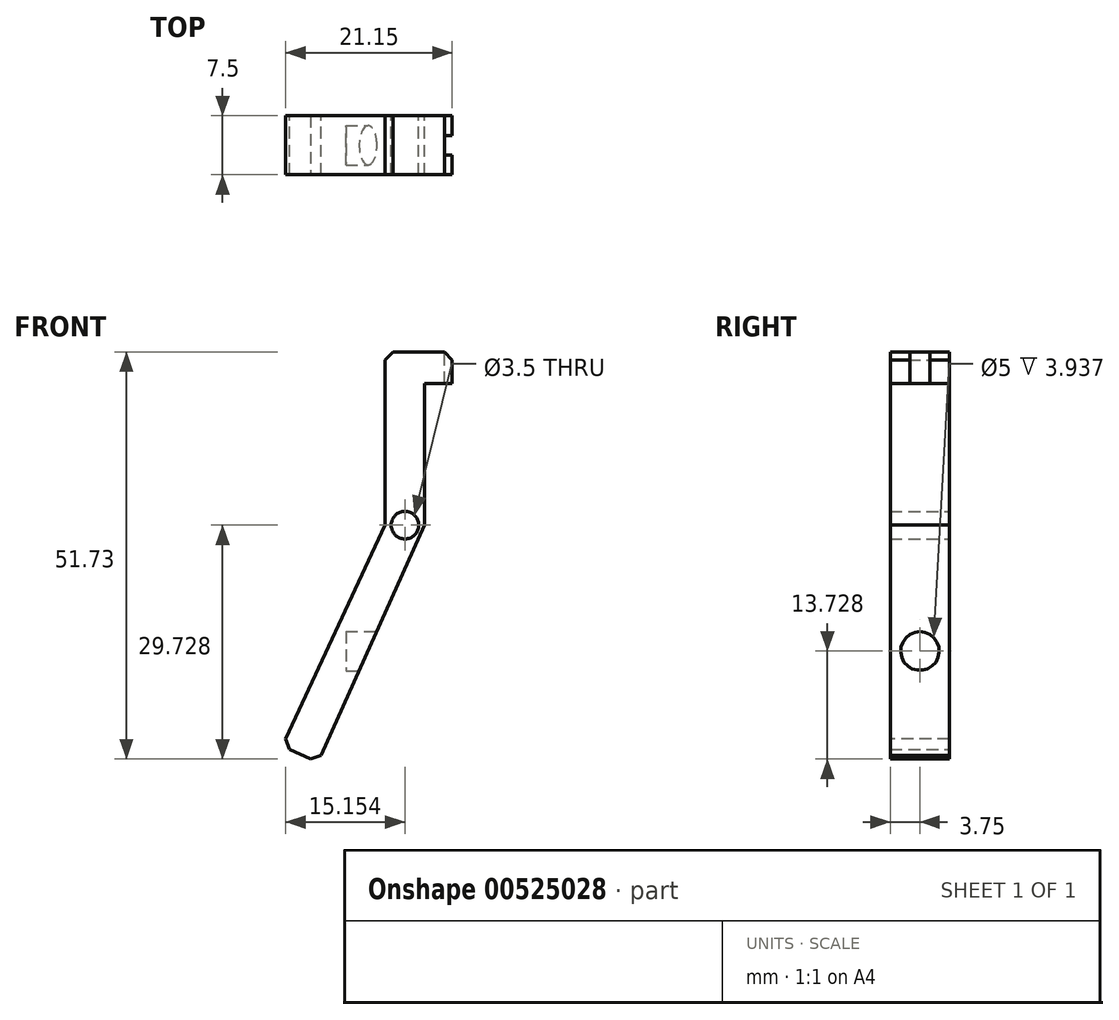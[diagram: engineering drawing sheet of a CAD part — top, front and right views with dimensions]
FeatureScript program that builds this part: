
annotation { "Feature Type Name" : "Feature", "Feature Type Description" : "" }
export const myFeature = defineFeature(function(context is Context, id is Id, definition is map)
    precondition{}
    {
        {
            var Q0;
            Q0=qCreatedBy(makeId("Front.planeOp"),FACE);
            var sketch = newSketch(context, id + "F0", { "sketchPlane" : qUnion([Q0])});
            skLineSegment(sketch, "E0", {"start": v(-25.66, -15.46) * mm, "end": v(-25.66, -11.46) * mm});
            skLineSegment(sketch, "E1", {"start": v(-25.66, -11.46) * mm, "end": v(-34.16, -11.46) * mm});
            skLineSegment(sketch, "E2", {"start": v(-34.16, -11.46) * mm, "end": v(-34.16, -33.46) * mm});
            skLineSegment(sketch, "E3", {"start": v(-29.16, -33.46) * mm, "end": v(-29.16, -15.46) * mm});
            skPoint(sketch, "E4.end.orphan", {"position": v(-21.37, -15.46) * mm});
            skLineSegment(sketch, "E5", {"start": v(-29.16, -15.46) * mm, "end": v(-25.66, -15.46) * mm});
            skPoint(sketch, "E6.center.orphan", {"position": v(-20.47, -41.23) * mm});
            skLineSegment(sketch, "E7", {"start": v(-34.16, -33.46) * mm, "end": v(-47.23, -61.5) * mm});
            skLineSegment(sketch, "E8", {"start": v(-47.23, -61.5) * mm, "end": v(-42.7, -63.62) * mm});
            skLineSegment(sketch, "E9", {"start": v(-42.7, -63.62) * mm, "end": v(-29.16, -33.46) * mm});
            skPoint(sketch, "E10.orphan", {"position": v(-34.16, -33.46) * mm});
            skCircle(sketch, "E11", {"center": v(-31.66, -33.46) * mm, "radius": 1.75 * mm});
            skSolve(sketch);
        }
        {
            var Q0;
            Q0 = qSketchRegion(id + "F0", true);
            extrude(context, id + "F1", {"entities" : qUnion([Q0]), "depth" : 7.5 * mm, "offsetDistance" : 25 * mm});
        }
        {
            var Q0;
            Q0=makeQuery(id+"F1.opExtrude","SWEPT_EDGE",EDGE,{"disambiguationData":[OSD([sQuery(id+"F0.wireOp",EDGE,"E1"),sQuery(id+"F0.wireOp",EDGE,"E2")])]});
            var Q1;
            Q1=makeQuery(id+"F1.opExtrude","SWEPT_EDGE",EDGE,{"disambiguationData":[OSD([sQuery(id+"F0.wireOp",EDGE,"E0"),sQuery(id+"F0.wireOp",EDGE,"E1")])]});
            var Q2;
            Q2=makeQuery(id+"F1.opExtrude","SWEPT_EDGE",EDGE,{"disambiguationData":[OSD([sQuery(id+"F0.wireOp",EDGE,"E8"),sQuery(id+"F0.wireOp",EDGE,"E9")])]});
            var Q3;
            Q3=makeQuery(id+"F1.opExtrude","SWEPT_EDGE",EDGE,{"disambiguationData":[OSD([sQuery(id+"F0.wireOp",EDGE,"E7"),sQuery(id+"F0.wireOp",EDGE,"E8")])]});
            chamfer(context, id + "F2", {"entities" : qUnion([Q0, Q1, Q2, Q3]), "width" : 1 * mm, "tangentPropagation" : true});
        }
        {
            var Q0;
            Q0=makeQuery(id+"F1.opExtrude","SWEPT_FACE",FACE,{"disambiguationData":[OSD([sQuery(id+"F0.wireOp",EDGE,"E2")])]});
            var sketch = newSketch(context, id + "F3", { "sketchPlane" : qUnion([Q0])});
            skCircle(sketch, "E12", {"center": v(3.75, -49.46) * mm, "radius": 2.5 * mm});
            skPoint(sketch, "E12.centerSnap0", {"position": v(3.75, -33.46) * mm});
            skSolve(sketch);
        }
        {
            var Q0;
            Q0=makeQuery(id+"F3.imprint","IMPRINT",FACE,{"disambiguationData":[TD([[makeQuery(id+"F3.imprint","IMPRINT",EDGE,{"derivedFrom":sQuery(id+"F3.wireOp",EDGE,"E12")}),1.0]])]});
            extrude(context, id + "F4", {"entities" : qUnion([Q0]), "operationType" : NewBodyOperationType.REMOVE, "depth" : 5 * mm, "offsetDistance" : 25 * mm});
        }
        {
            var Q0;
            Q0=makeQuery(id+"F1.opExtrude","SWEPT_FACE",FACE,{"disambiguationData":[OSD([sQuery(id+"F0.wireOp",EDGE,"E0")])]});
            var sketch = newSketch(context, id + "F5", { "sketchPlane" : qUnion([Q0])});
            skLineSegment(sketch, "E13", {"start": v(-5, -15.46) * mm, "end": v(-5, -12.46) * mm});
            skLineSegment(sketch, "E14", {"start": v(-5, -12.46) * mm, "end": v(-2.5, -12.46) * mm});
            skLineSegment(sketch, "E15", {"start": v(-2.5, -12.46) * mm, "end": v(-2.5, -15.46) * mm});
            skLineSegment(sketch, "E16", {"start": v(-2.5, -15.46) * mm, "end": v(-3.72, -15.45) * mm});
            skSolve(sketch);
        }
        {
            var Q0;
            {var subQ0=sQuery(id+"F5.wireOp",EDGE,"E13");Q0=makeQuery(id+"F5.imprint","IMPRINT",FACE,{"disambiguationData":[TD([[makeQuery(id+"F5.imprint","IMPRINT",EDGE,{"derivedFrom":subQ0}),-1.0]])]});}
            extrude(context, id + "F6", {"entities" : qUnion([Q0]), "operationType" : NewBodyOperationType.REMOVE, "oppositeDirection" : true, "depth" : 1 * mm, "offsetDistance" : 25 * mm});
        }
        {
            var Q0;
            Q0=makeQuery(id+"F6.boolean.opBoolean","COPY",FACE,{"derivedFrom":makeQuery(id+"F6.opExtrude","SWEPT_FACE",FACE,{"disambiguationData":[OSD([sQuery(id+"F5.wireOp",EDGE,"E14")])]})});
            var sketch = newSketch(context, id + "F7", { "sketchPlane" : qUnion([Q0])});
            skLineSegment(sketch, "E17", {"start": v(-25.66, 5) * mm, "end": v(-25.66, 2.5) * mm});
            skLineSegment(sketch, "E18", {"start": v(-25.66, 2.5) * mm, "end": v(-26.66, 2.5) * mm});
            skLineSegment(sketch, "E19", {"start": v(-26.66, 2.5) * mm, "end": v(-26.66, 5) * mm});
            skLineSegment(sketch, "E20", {"start": v(-26.66, 5) * mm, "end": v(-25.66, 5) * mm});
            skSolve(sketch);
        }
        {
            var Q0;
            Q0=makeQuery(id+"F7.imprint","IMPRINT",FACE,{"disambiguationData":[TD([[makeQuery(id+"F7.imprint","IMPRINT",EDGE,{"derivedFrom":sQuery(id+"F7.wireOp",EDGE,"E17")}),1.0]])]});
            extrude(context, id + "F8", {"entities" : qUnion([Q0]), "operationType" : NewBodyOperationType.REMOVE, "oppositeDirection" : true, "depth" : 25 * mm, "offsetDistance" : 25 * mm});
        }
    });
